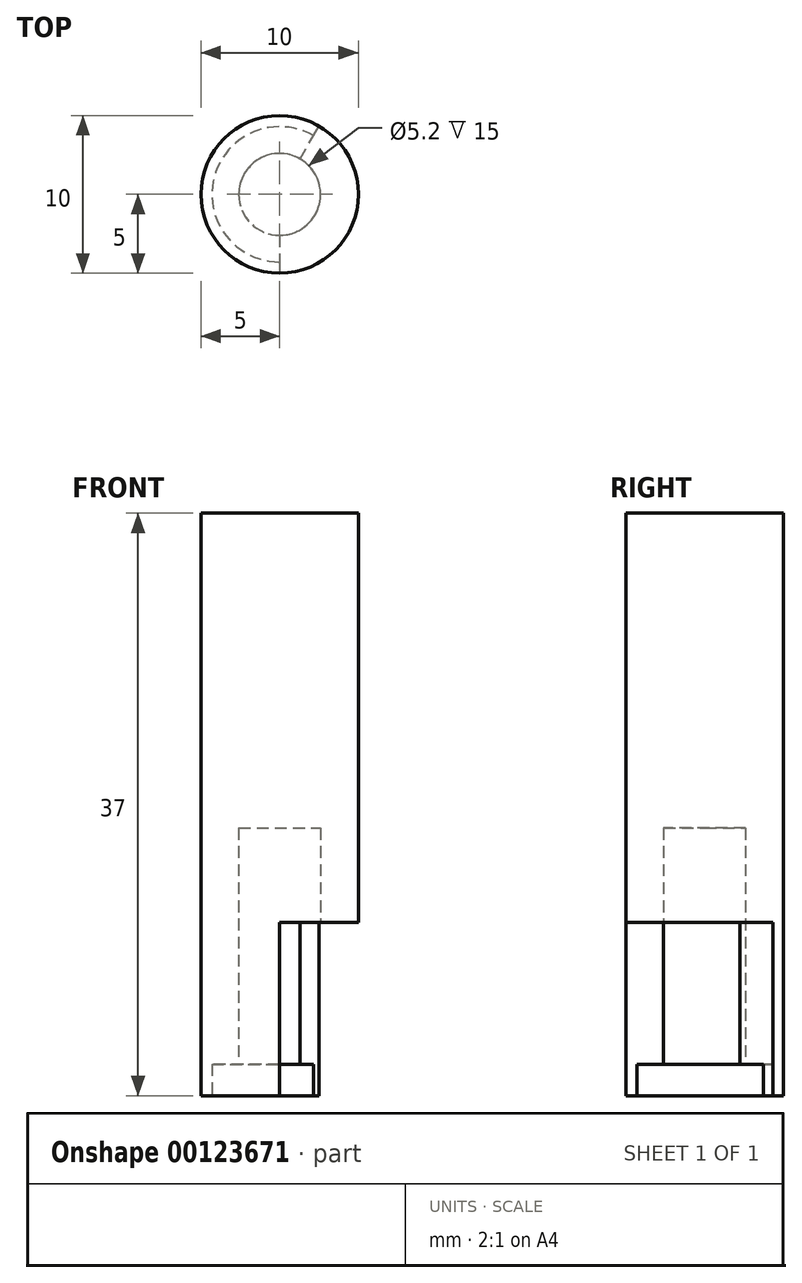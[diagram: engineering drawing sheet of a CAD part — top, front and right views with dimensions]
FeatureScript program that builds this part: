
annotation { "Feature Type Name" : "Feature", "Feature Type Description" : "" }
export const myFeature = defineFeature(function(context is Context, id is Id, definition is map)
    precondition{}
    {
        {
            var Q0;
            Q0=qCreatedBy(makeId("Top.planeOp"),FACE);
            var sketch = newSketch(context, id + "F0", { "sketchPlane" : qUnion([Q0])});
            skCircle(sketch, "E0", {"center": v(0, 0) * mm, "radius": 5 * mm});
            skSolve(sketch);
        }
        {
            var Q0;
            Q0 = qSketchRegion(id + "F0", true);
            extrude(context, id + "F1", {"entities" : qUnion([Q0]), "depth" : 37 * mm});
        }
        {
            var Q0;
            Q0=makeQuery(id+"F1.opExtrude","CAP_FACE",FACE,{"disambiguationData":[OSD([sQuery(id+"F0.wireOp",EDGE,"E0"),sQuery(id+"F0.wireOp",EDGE,"UcMSlVTw-qX6Q-l4Zu-FFFh-LXO7WUimJ8u3")])],"isStart":true});
            var sketch = newSketch(context, id + "F2", { "sketchPlane" : qUnion([Q0])});
            skCircle(sketch, "E1", {"center": v(0, 0) * mm, "radius": 4.3 * mm});
            skSolve(sketch);
        }
        {
            var Q0;
            Q0 = qSketchRegion(id + "F2", true);
            extrude(context, id + "F3", {"entities" : qUnion([Q0]), "operationType" : NewBodyOperationType.REMOVE, "oppositeDirection" : true, "depth" : 2 * mm});
        }
        {
            var Q0;
            Q0=makeQuery(id+"F3.boolean.opBoolean","COPY",FACE,{"derivedFrom":makeQuery(id+"F3.opExtrude","CAP_FACE",FACE,{"disambiguationData":[OSD([sQuery(id+"F2.wireOp",EDGE,"E1")])],"isStart":false})});
            var sketch = newSketch(context, id + "F4", { "sketchPlane" : qUnion([Q0])});
            skCircle(sketch, "E2", {"center": v(0, 0) * mm, "radius": 2.6 * mm});
            skSolve(sketch);
        }
        {
            var Q0;
            Q0 = qSketchRegion(id + "F4", true);
            extrude(context, id + "F5", {"entities" : qUnion([Q0]), "operationType" : NewBodyOperationType.REMOVE, "oppositeDirection" : true, "depth" : 15 * mm});
        }
        {
            var Q0;
            Q0=makeQuery(id+"F1.opExtrude","CAP_FACE",FACE,{"disambiguationData":[OSD([sQuery(id+"F0.wireOp",EDGE,"E0"),sQuery(id+"F0.wireOp",EDGE,"UcMSlVTw-qX6Q-l4Zu-FFFh-LXO7WUimJ8u3")])],"isStart":true});
            var sketch = newSketch(context, id + "F6", { "sketchPlane" : qUnion([Q0])});
            skLineSegment(sketch, "E3", {"start": v(0, 0) * mm, "end": v(0, 5) * mm});
            skLineSegment(sketch, "E4", {"start": v(0, 0) * mm, "end": v(2.5, -4.33) * mm});
            skArc(sketch, "E5", {"start": v(2.5, -4.33) * mm, "mid": v(4.83, 1.3) * mm, "end": v(0, 5) * mm});
            skSolve(sketch);
        }
        {
            var Q0;
            Q0 = qSketchRegion(id + "F6", true);
            var Q1;
            Q1=makeQuery(id+"F5.boolean.opBoolean","COPY",FACE,{"derivedFrom":makeQuery(id+"F5.opExtrude","CAP_FACE",FACE,{"disambiguationData":[OSD([sQuery(id+"F4.wireOp",EDGE,"E2")])],"isStart":false})});
            extrude(context, id + "F7", {"entities" : qUnion([Q0]), "operationType" : NewBodyOperationType.REMOVE, "oppositeDirection" : true, "endBoundEntityFace" : qUnion([Q1]), "depth" : 11 * mm});
        }
    });
